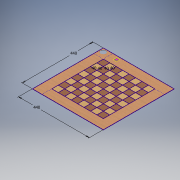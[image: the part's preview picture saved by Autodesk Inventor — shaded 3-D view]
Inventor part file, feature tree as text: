
AUTODESK INVENTOR PART (.ipt)
format: ipt  version: 2019 (Build 230136000, 136)  size: 486,912 bytes
history: native  units: in
note: dims shown in document units (in); Inventor stores cm internally (conversion verified against a paired STEP export)
features: extrude x5, sketch x3, plane x1
ambient origin geometry x8: Origin, YZ Plane, XZ Plane, XY Plane, X Axis, Y Axis, Z Axis, Center Point
bodies: Solid3 (feature_tree), Solid4 (feature_tree)
feature tree (9):
  plane  "Work Plane4"
  sketch  "Sketch2"  dims[d4=1.5748in d5=1.5748in]
  extrude  "Extrusion2"  Depth=1.5748in
  extrude  "Extrusion3"  Depth=17.3228in
  extrude  "Extrusion4"  Depth=0.1181in TaperAngle=0.0deg
  extrude  "Extrusion5"  Depth=0.0787in TaperAngle=0.0deg
  extrude  "Extrusion6"  Depth=0.0787in TaperAngle=0.0deg
  sketch  "Sketch3"  dims[d6=3.1496in d8=1.5748in d9=3.1496in d11=1.5748in d14=17.3228in]
  sketch  "Sketch4"  dims[d15=17.3228in d16=0.1181in d17=0.0in d18=0.0787in d19=0.0in d20=0.0787in d21=0.0in d22=0.9843in d25=0.3937in d26=0.0in d32=13.7795in d34=0.689in d35=0.2067in d37=0.3937in d38=0.2067in d39=0.2067in d40=0.2067in d41=0.3937in d42=0.0in]
